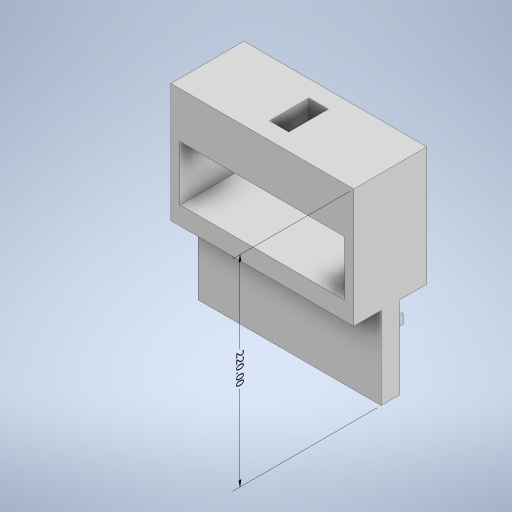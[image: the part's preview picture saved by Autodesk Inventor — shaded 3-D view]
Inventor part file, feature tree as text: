
AUTODESK INVENTOR PART (.ipt)
format: ipt  version: 2023 (Build 270158000, 158)  size: 307,200 bytes
history: native  units: mm
features: extrude x6, sketch x6, other x4, plane x2
ambient origin geometry x8: Origin, YZ Plane, XZ Plane, XY Plane, X Axis, Y Axis, Z Axis, Center Point
bodies: Body1 (feature_tree), Body2 (feature_tree)
feature tree (18):
  other  "Sólido1"
  other  "Anotaciones"
  extrude  "Extrusión1"  Depth=80.0mm
  extrude  "Extrusión2"  Depth=180.0mm
  extrude  "Extrusión3"  Depth=20.0mm
  extrude  "Extrusión4"  Depth=21.0mm
  plane  "Plano de trabajo1"
  extrude  "Extrusión6"  Depth=20.0mm
  plane  "Plano de trabajo3"
  extrude  "Extrusión7"  [1 undecoded]
  sketch  "Boceto1"  dims[d0=200.0mm d1=80.0mm]
  sketch  "Boceto2"  dims[d2=130.0mm d3=0.0mm d4=180.0mm]
  sketch  "Boceto3"  dims[d5=60.0mm d6=20.0mm]
  sketch  "Boceto4"  dims[d7=60.0mm d8=0.0mm d9=21.0mm d10=43.0mm]
  sketch  "Boceto7"  dims[d11=43.0mm d12=0.0mm d13=20.0mm]
  other  "Sólido3"
  sketch  "Boceto10"  dims[d14=90.0mm d15=0.0mm d16=-90.0mm d28=20.0mm d29=20.0mm d30=30.0mm d31=30.0mm d32=20.0mm d33=35.0mm d34=35.0mm d35=69.0mm d36=10.0mm d37=0.0mm d45=1.5mm d50=10.0mm d51=0.0mm d52=10.0mm d53=89.5mm d38=3.166395mm d39=4.283575mm d40=220.0mm]
  other  "Cota lineal 1"
note: 1 required parameter value undecoded (feature->parameter linkage not recoverable at this tier; creation-order binding heuristic only, values carry confidence <= 0.55)
